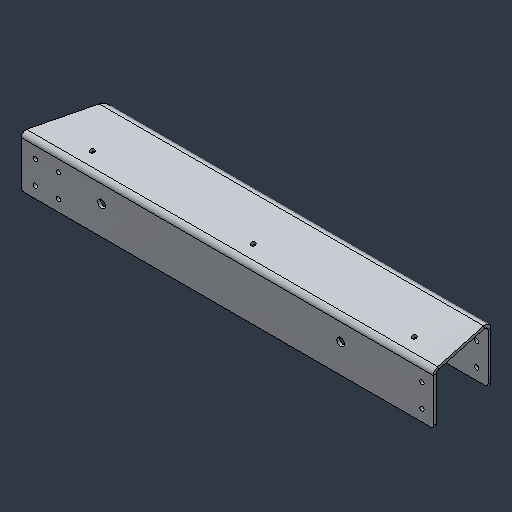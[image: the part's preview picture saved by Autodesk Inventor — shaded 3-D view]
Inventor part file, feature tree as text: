
AUTODESK INVENTOR PART (.ipt)
format: ipt  version: 2024.3 (Build 283343000, 343)  size: 143,872 bytes
history: native  units: mm (DEFAULTED — no unit token found)
features: fillet x1
ambient origin geometry x8: Origin, YZ Plane, XZ Plane, XY Plane, X Axis, Y Axis, Z Axis, Center Point
bodies: Solid1 (feature_tree)
feature tree (1):
  fillet  "Fillet1"  [1 undecoded]
note: 1 required parameter value undecoded (feature->parameter linkage not recoverable at this tier; creation-order binding heuristic only, values carry confidence <= 0.55)
